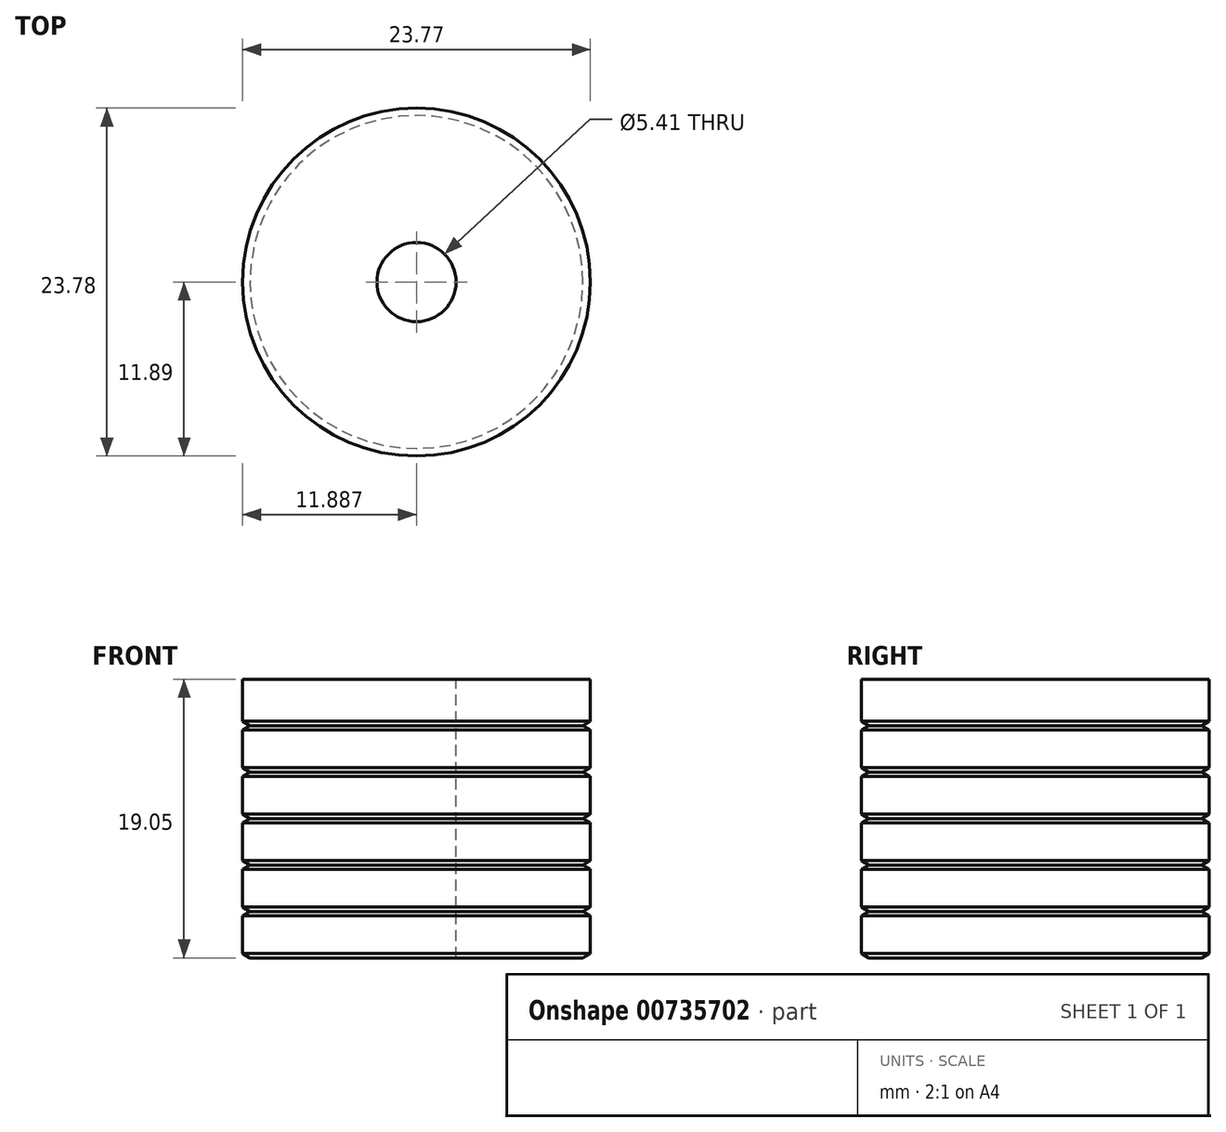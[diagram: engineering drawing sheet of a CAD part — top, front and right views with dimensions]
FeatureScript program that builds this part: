
annotation { "Feature Type Name" : "Feature", "Feature Type Description" : "" }
export const myFeature = defineFeature(function(context is Context, id is Id, definition is map)
    precondition{}
    {
        {
            var Q0;
            Q0=qCreatedBy(makeId("Front.planeOp"),FACE);
            var sketch = newSketch(context, id + "F0", { "sketchPlane" : qUnion([Q0])});
            skLineSegment(sketch, "E0.bottom", {"start": v(0, 0) * mm, "end": v(11.89, 0) * mm});
            skLineSegment(sketch, "E0.top", {"start": v(0, 19.05) * mm, "end": v(11.89, 19.05) * mm});
            skLineSegment(sketch, "E0.left", {"start": v(0, 0) * mm, "end": v(0, 19.05) * mm});
            skLineSegment(sketch, "E1", {"start": v(11.89, 3.18) * mm, "end": v(0.5, 3.18) * mm});
            skLineSegment(sketch, "E2", {"start": v(11.89, 6.35) * mm, "end": v(0.5, 6.35) * mm});
            skLineSegment(sketch, "E3", {"start": v(11.89, 9.53) * mm, "end": v(0.5, 9.53) * mm});
            skLineSegment(sketch, "E4", {"start": v(11.89, 12.7) * mm, "end": v(0.5, 12.7) * mm});
            skLineSegment(sketch, "E5", {"start": v(11.89, 15.88) * mm, "end": v(0.5, 15.88) * mm});
            skPoint(sketch, "E6", {"position": v(0.5, 15.87) * mm});
            skLineSegment(sketch, "E7", {"start": v(0.5, 15.87) * mm, "end": v(0, 16.17) * mm});
            skLineSegment(sketch, "E8", {"start": v(0.5, 15.88) * mm, "end": v(0, 15.58) * mm});
            skPoint(sketch, "E9.orphan", {"position": v(0, 15.88) * mm});
            skLineSegment(sketch, "E10", {"start": v(0, 16.17) * mm, "end": v(11.89, 16.17) * mm});
            skLineSegment(sketch, "E11", {"start": v(0, 15.58) * mm, "end": v(11.89, 15.58) * mm});
            skPoint(sketch, "E12", {"position": v(0.5, 6.35) * mm});
            skPoint(sketch, "E13", {"position": v(0.5, 3.17) * mm});
            skPoint(sketch, "E14", {"position": v(0.5, 0) * mm});
            skPoint(sketch, "E15", {"position": v(0.5, 9.53) * mm});
            skPoint(sketch, "E16", {"position": v(0.5, 12.7) * mm});
            skLineSegment(sketch, "E17", {"start": v(0.5, 12.7) * mm, "end": v(0, 13) * mm});
            skLineSegment(sketch, "E18", {"start": v(0.5, 12.7) * mm, "end": v(0, 12.4) * mm});
            skLineSegment(sketch, "E19", {"start": v(0.5, 9.53) * mm, "end": v(0, 9.82) * mm});
            skLineSegment(sketch, "E20", {"start": v(0.5, 9.53) * mm, "end": v(0, 9.23) * mm});
            skLineSegment(sketch, "E21", {"start": v(0.5, 6.35) * mm, "end": v(0, 6.64) * mm});
            skLineSegment(sketch, "E22", {"start": v(0.5, 6.35) * mm, "end": v(0, 6.06) * mm});
            skLineSegment(sketch, "E23", {"start": v(0.5, 3.17) * mm, "end": v(0, 3.47) * mm});
            skLineSegment(sketch, "E24", {"start": v(0.5, 3.17) * mm, "end": v(0, 2.88) * mm});
            skLineSegment(sketch, "E25", {"start": v(0.5, 0) * mm, "end": v(0, 0.3) * mm});
            skLineSegment(sketch, "E26", {"start": v(0, 13) * mm, "end": v(11.89, 13) * mm});
            skLineSegment(sketch, "E27", {"start": v(0, 12.4) * mm, "end": v(11.89, 12.4) * mm});
            skLineSegment(sketch, "E28", {"start": v(0, 9.82) * mm, "end": v(11.89, 9.82) * mm});
            skLineSegment(sketch, "E29", {"start": v(0, 9.23) * mm, "end": v(11.89, 9.23) * mm});
            skLineSegment(sketch, "E30", {"start": v(0, 6.64) * mm, "end": v(11.89, 6.64) * mm});
            skLineSegment(sketch, "E31", {"start": v(0, 6.06) * mm, "end": v(11.89, 6.06) * mm});
            skLineSegment(sketch, "E32", {"start": v(0, 3.47) * mm, "end": v(11.89, 3.47) * mm});
            skLineSegment(sketch, "E33", {"start": v(0, 2.88) * mm, "end": v(11.89, 2.88) * mm});
            skPoint(sketch, "E34.orphan", {"position": v(0, 12.7) * mm});
            skPoint(sketch, "E35.orphan", {"position": v(0, 9.53) * mm});
            skLineSegment(sketch, "E36", {"start": v(0, 0.3) * mm, "end": v(11.89, 0.3) * mm});
            skLineSegment(sketch, "E37", {"start": v(11.89, 19.05) * mm, "end": v(11.89, 0) * mm});
            skSolve(sketch);
        }
        {
            var Q0;
            {var subQ0=sQuery(id+"F0.wireOp",EDGE,"E0.top");Q0=makeQuery(id+"F0.imprint","IMPRINT",FACE,{"disambiguationData":[TD([[makeQuery(id+"F0.imprint","IMPRINT",EDGE,{"derivedFrom":subQ0}),-1.0]])]});}
            var Q1;
            {var subQ0=sQuery(id+"F0.wireOp",EDGE,"E5");Q1=makeQuery(id+"F0.imprint","IMPRINT",FACE,{"disambiguationData":[TD([[makeQuery(id+"F0.imprint","IMPRINT",EDGE,{"derivedFrom":subQ0}),-1.0]])]});}
            var Q2;
            {var subQ0=sQuery(id+"F0.wireOp",EDGE,"E5");Q2=makeQuery(id+"F0.imprint","IMPRINT",FACE,{"disambiguationData":[TD([[makeQuery(id+"F0.imprint","IMPRINT",EDGE,{"derivedFrom":subQ0}),1.0]])]});}
            var Q3;
            {var subQ0=sQuery(id+"F0.wireOp",EDGE,"E11");Q3=makeQuery(id+"F0.imprint","IMPRINT",FACE,{"disambiguationData":[TD([[makeQuery(id+"F0.imprint","IMPRINT",EDGE,{"derivedFrom":subQ0}),-1.0]])]});}
            var Q4;
            {var subQ0=sQuery(id+"F0.wireOp",EDGE,"E4");Q4=makeQuery(id+"F0.imprint","IMPRINT",FACE,{"disambiguationData":[TD([[makeQuery(id+"F0.imprint","IMPRINT",EDGE,{"derivedFrom":subQ0}),-1.0]])]});}
            var Q5;
            {var subQ0=sQuery(id+"F0.wireOp",EDGE,"E4");Q5=makeQuery(id+"F0.imprint","IMPRINT",FACE,{"disambiguationData":[TD([[makeQuery(id+"F0.imprint","IMPRINT",EDGE,{"derivedFrom":subQ0}),1.0]])]});}
            var Q6;
            {var subQ0=sQuery(id+"F0.wireOp",EDGE,"E27");Q6=makeQuery(id+"F0.imprint","IMPRINT",FACE,{"disambiguationData":[TD([[makeQuery(id+"F0.imprint","IMPRINT",EDGE,{"derivedFrom":subQ0}),-1.0]])]});}
            var Q7;
            {var subQ0=sQuery(id+"F0.wireOp",EDGE,"E3");Q7=makeQuery(id+"F0.imprint","IMPRINT",FACE,{"disambiguationData":[TD([[makeQuery(id+"F0.imprint","IMPRINT",EDGE,{"derivedFrom":subQ0}),-1.0]])]});}
            var Q8;
            {var subQ0=sQuery(id+"F0.wireOp",EDGE,"E3");Q8=makeQuery(id+"F0.imprint","IMPRINT",FACE,{"disambiguationData":[TD([[makeQuery(id+"F0.imprint","IMPRINT",EDGE,{"derivedFrom":subQ0}),1.0]])]});}
            var Q9;
            {var subQ0=sQuery(id+"F0.wireOp",EDGE,"E29");Q9=makeQuery(id+"F0.imprint","IMPRINT",FACE,{"disambiguationData":[TD([[makeQuery(id+"F0.imprint","IMPRINT",EDGE,{"derivedFrom":subQ0}),-1.0]])]});}
            var Q10;
            {var subQ0=sQuery(id+"F0.wireOp",EDGE,"E2");Q10=makeQuery(id+"F0.imprint","IMPRINT",FACE,{"disambiguationData":[TD([[makeQuery(id+"F0.imprint","IMPRINT",EDGE,{"derivedFrom":subQ0}),-1.0]])]});}
            var Q11;
            {var subQ0=sQuery(id+"F0.wireOp",EDGE,"E2");Q11=makeQuery(id+"F0.imprint","IMPRINT",FACE,{"disambiguationData":[TD([[makeQuery(id+"F0.imprint","IMPRINT",EDGE,{"derivedFrom":subQ0}),1.0]])]});}
            var Q12;
            {var subQ0=sQuery(id+"F0.wireOp",EDGE,"E31");Q12=makeQuery(id+"F0.imprint","IMPRINT",FACE,{"disambiguationData":[TD([[makeQuery(id+"F0.imprint","IMPRINT",EDGE,{"derivedFrom":subQ0}),-1.0]])]});}
            var Q13;
            {var subQ0=sQuery(id+"F0.wireOp",EDGE,"E1");Q13=makeQuery(id+"F0.imprint","IMPRINT",FACE,{"disambiguationData":[TD([[makeQuery(id+"F0.imprint","IMPRINT",EDGE,{"derivedFrom":subQ0}),-1.0]])]});}
            var Q14;
            {var subQ0=sQuery(id+"F0.wireOp",EDGE,"E1");Q14=makeQuery(id+"F0.imprint","IMPRINT",FACE,{"disambiguationData":[TD([[makeQuery(id+"F0.imprint","IMPRINT",EDGE,{"derivedFrom":subQ0}),1.0]])]});}
            var Q15;
            {var subQ0=sQuery(id+"F0.wireOp",EDGE,"E33");Q15=makeQuery(id+"F0.imprint","IMPRINT",FACE,{"disambiguationData":[TD([[makeQuery(id+"F0.imprint","IMPRINT",EDGE,{"derivedFrom":subQ0}),-1.0]])]});}
            var Q16;
            {var subQ3=sQuery(id+"F0.wireOp",EDGE,"E25");Q16=makeQuery(id+"F0.imprint","IMPRINT",FACE,{"disambiguationData":[TD([[makeQuery(id+"F0.imprint","IMPRINT",EDGE,{"derivedFrom":subQ3}),-1.0]])]});}
            var Q17;
            Q17=sQuery(id+"F0.wireOp",EDGE,"E37");
            revolve(context, id + "F1", {"surfaceOperationType" : NewSurfaceOperationType.NEW, "entities" : qUnion([Q0, Q1, Q2, Q3, Q4, Q5, Q6, Q7, Q8, Q9, Q10, Q11, Q12, Q13, Q14, Q15, Q16]), "axis" : qUnion([Q17]), "revolveType" : RevolveType.FULL});
        }
        {
            var Q0;
            Q0=makeQuery(id+"F1.opRevolve","SWEPT_FACE",FACE,{"disambiguationData":[OSD([sQuery(id+"F0.wireOp",EDGE,"E0.top")])]});
            var sketch = newSketch(context, id + "F2", { "sketchPlane" : qUnion([Q0])});
            skCircle(sketch, "E38", {"center": v(11.89, 0) * mm, "radius": 2.7 * mm});
            skSolve(sketch);
        }
        {
            var Q0;
            Q0 = qSketchRegion(id + "F2", true);
            extrude(context, id + "F3", {"entities" : qUnion([Q0]), "operationType" : NewBodyOperationType.REMOVE, "endBound" : BoundingType.UP_TO_NEXT, "oppositeDirection" : true, "depth" : 25.4 * mm, "offsetDistance" : 25.4 * mm});
        }
    });
